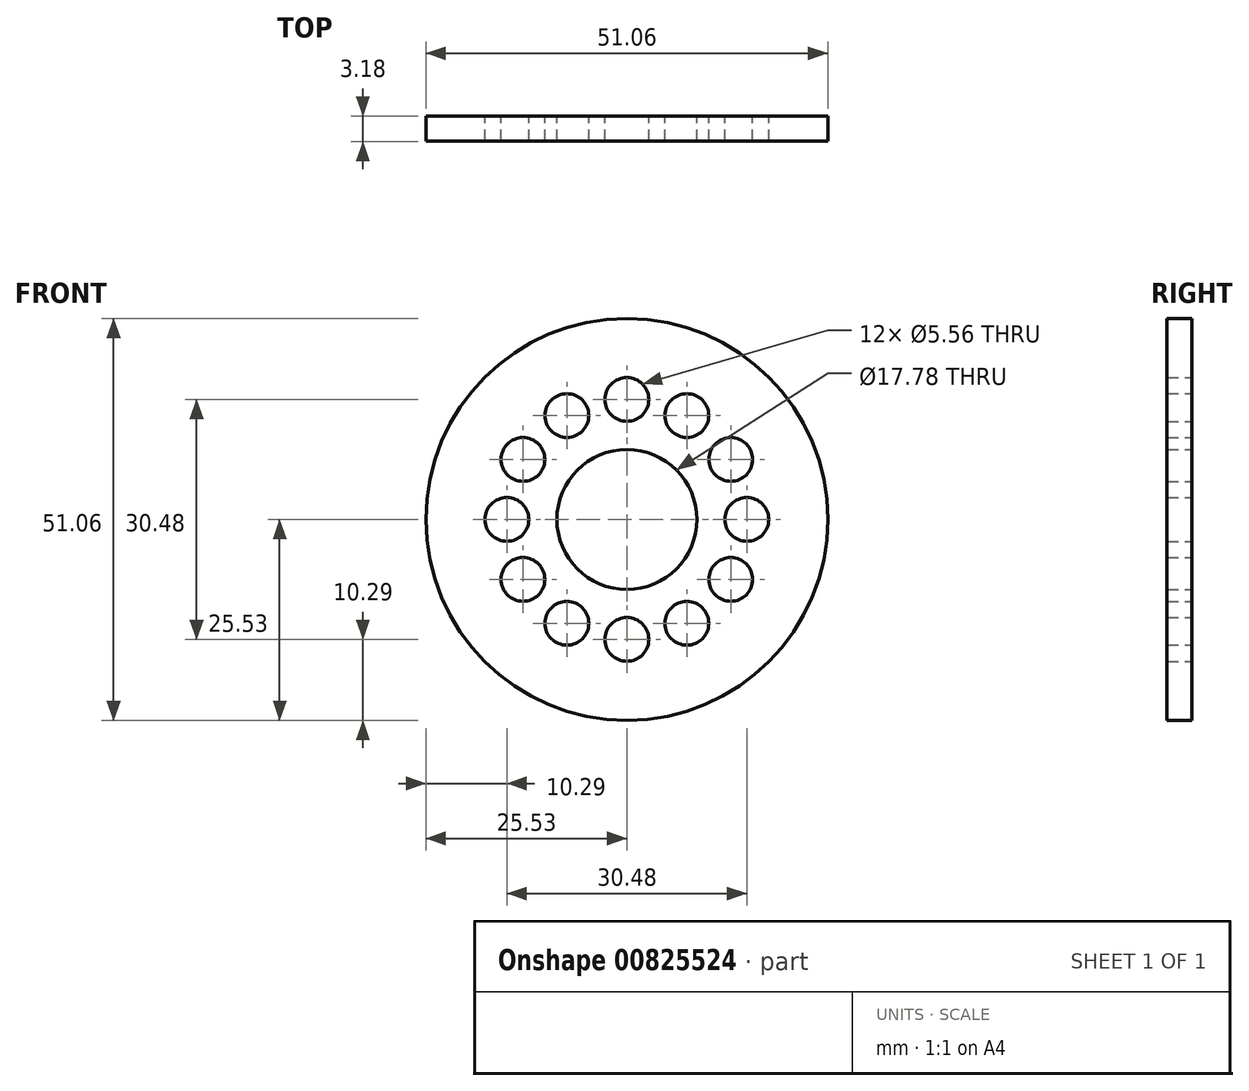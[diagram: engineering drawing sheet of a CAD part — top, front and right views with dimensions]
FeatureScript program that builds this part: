
annotation { "Feature Type Name" : "Feature", "Feature Type Description" : "" }
export const myFeature = defineFeature(function(context is Context, id is Id, definition is map)
    precondition{}
    {
        {
            var Q0;
            Q0=qCreatedBy(makeId("Front.planeOp"),FACE);
            var sketch = newSketch(context, id + "F0", { "sketchPlane" : qUnion([Q0])});
            skCircle(sketch, "E0", {"center": v(0, 0) * mm, "radius": 25.53 * mm});
            skCircle(sketch, "E1", {"center": v(0, 15.24) * mm, "radius": 2.78 * mm});
            skCircle(sketch, "E2", {"center": v(0, 0) * mm, "radius": 8.9 * mm});
            skLineSegment(sketch, "E3", {"start": v(0, 15.24) * mm, "end": v(0, 0) * mm});
            skCircle(sketch, "E4.1.0", {"center": v(-7.62, 13.2) * mm, "radius": 2.78 * mm});
            skCircle(sketch, "E4.2.0", {"center": v(-13.2, 7.62) * mm, "radius": 2.78 * mm});
            skCircle(sketch, "E4.3.0", {"center": v(-15.24, 0) * mm, "radius": 2.78 * mm});
            skCircle(sketch, "E4.4.0", {"center": v(-13.2, -7.62) * mm, "radius": 2.78 * mm});
            skCircle(sketch, "E4.5.0", {"center": v(-7.62, -13.2) * mm, "radius": 2.78 * mm});
            skCircle(sketch, "E4.6.0", {"center": v(0, -15.24) * mm, "radius": 2.78 * mm});
            skCircle(sketch, "E4.7.0", {"center": v(7.62, -13.2) * mm, "radius": 2.78 * mm});
            skCircle(sketch, "E4.8.0", {"center": v(13.2, -7.62) * mm, "radius": 2.78 * mm});
            skCircle(sketch, "E4.9.0", {"center": v(15.24, 0) * mm, "radius": 2.78 * mm});
            skCircle(sketch, "E4.10.0", {"center": v(13.2, 7.62) * mm, "radius": 2.78 * mm});
            skCircle(sketch, "E4.11.0", {"center": v(7.62, 13.2) * mm, "radius": 2.78 * mm});
            skSolve(sketch);
        }
        {
            var Q0;
            Q0 = qSketchRegion(id + "F0", true);
            extrude(context, id + "F1", {"entities" : qUnion([Q0]), "depth" : 3.17 * mm, "offsetDistance" : 25.4 * mm});
        }
    });
